# Revit family: Zumtobel VAERO LED
name_source: partatom
category: Lighting Fixtures
revit_build: Autodesk Revit 2014 (Build: 20140709_2115(x64)
units: mm (PartAtom-declared; Revit-internal decimal feet)

## types (2) — shared parameters
Assembly Code = D5020210
Body = Zumtobel_Metal_Aluminium
Color Filter = 16777215
Description = LED suspended luminaire
Dimming Lamp Color Temperature Shift = <None>
Emit Shape Visible in Rendering = No
Emit from Rectangle Length = 365 mm  [stored 1.19751 ft]
Emit from Rectangle Width = 1250 mm  [stored 4.10105 ft]
Height = 45 mm  [stored 0.147638 ft]
Lamp = LED
Length = 1250 mm  [stored 4.10105 ft]
Manufacturer = Zumtobel Lighting
Suspension = Zumtobel_Metal_Aluminium
Tilt Angle = -90.00°
URL = http://www.zumtobel.com
Voltage = 230 V
Waveguide = Zumtobel_Waveguide_Self_Illumination
Width = 365 mm  [stored 1.19751 ft]
zero-valued in all types: Default Elevation

## per-type parameters (varying)
| type | Apparent Load | Model | Photometric Web File |
| VAERO LED5000 | 47 VA | 42184828 | 42184828_(STD).IES |
| VAERO LED6600 | 63 VA | 42184830 | 42184830_(STD).IES |

note: [stored X ft] marks values corroborated as IEEE doubles in the binary element streams (Revit-internal decimal feet)

## geometry (parser evidence)
native form markers: Sweep x4
no freeform markers — native parametric forms only
